# Revit family: CONV_Pholc_GnrlPrpseLmnrs_Bounce116
name_source: partatom
category: Lighting Fixtures
revit_build: Autodesk Revit 2017 (Build: 20181011_1645(x64)
units: mm (PartAtom-declared; Revit-internal decimal feet)

## family parameters
Always vertical = Yes
Cut with Voids When Loaded = No
Host = Ceiling
Light Source = No
OmniClass Number = 23.80.70.11
OmniClass Title = Luminaries for Internal Lighting
Part Type = Normal
Room Calculation Point = No
Round Connector Dimension = Use Diameter
Shared = No

## types (1)
- Bounce 116 black/opal glass
    Apparent Load = 0 VA
    ArticleNumber = 514165
    AssetType = Fixed
    BIMObjectName = CONV_Pholc_GnrlPrpseLmnrs_Bounce116
    Brand = Pholc
    Category = Pendant
    Collection = Bounce
    Color = Various
    ConvergoRefNr = 0103-1905-0004-SE
    DefaultElevation = 0 mm  [stored 0 ft]
    Description = The pattern that Bounce creates is energetic, graphic and bouncy. A positive graphic feeling. I wanted to create a lamp that gives the room character and at the same time gives light. With that in mind, I created a graphic expression with a focus on the path the electricity is drawn from light spot to light spot. The result is a flat, screen-like luminaire that fits well over oblong tables or counters.
    Designer = Monika Mulder
    DurationUnit = Year
    ElectricalDeviceNominalPower = 20 W
    Features = G9 base socket. Suspension mounting. Black textile cable. Black metal ceiling cup.
    HasProtectiveEarth = No
    IP_Code = IP 20
    IfcExportAs = IfcLightFixtureType
    IfcExportType = NOTDEFINED
    InsulationStandardClass = Class I
    LensMaterial = Opal glass
    LightFixtureMainMaterial = Black metal
    LightFixtureMountingType = Suspended
    LightFixturePlacingType = Ceiling
    LightFixtureSecondaryMaterial = Black
    MaintenanceFactor = 0
    Manufacturer = Pholc
    ManufacturerName = Pholc
    ManufacturerURL = https://www.pholc.se
    Material = Metal, opal glass & textile
    Model = Bounce 116 black/opal glass
    ModelReference = 514165
    NBSDescription = General purpose luminaires
    NBSReference = 90-60-50/405
    Name = GnrlPrpseLmnrs_Bounce116
    NominalCurrent = 0 A
    NominalDepth = 110 mm  [stored 0.360892 ft]
    NominalFrequencyRange = 50 Hz
    NominalLength = 1160 mm  [stored 3.80577 ft]
    NominalVoltage = 220 V
    NominalVoltageCalc = 0 V
    NumberOfPoles = 1
    NumberOfSources = 6
    PhaseAngle = 0.00°
    ProductDatasheet = https://www.pholc.se
    ProductInformation = The pattern that Bounce creates is energetic, graphic and bouncy. A positive graphic feeling.
    Shape = Sculptured
    Size = 1160x110x650 mm
    TotalWattage = 120 W
    URL = https://www.pholc.se
    Uniclass2 = Pr_70_70_49_86
    Uniclass2015Description = Suspended luminaires
    Uniclass2015Reference = Pr_70_70_48_86
    UsageCurrent = 0 A
    Version = 1
    VersionDate = 14/05/2019
    WarrantyDurationUnit = Year
    Weight = 3.1 kg

note: [stored X ft] marks values corroborated as IEEE doubles in the binary element streams (Revit-internal decimal feet)

## geometry (parser evidence)
native form markers: Sweep x10
no freeform markers — native parametric forms only
